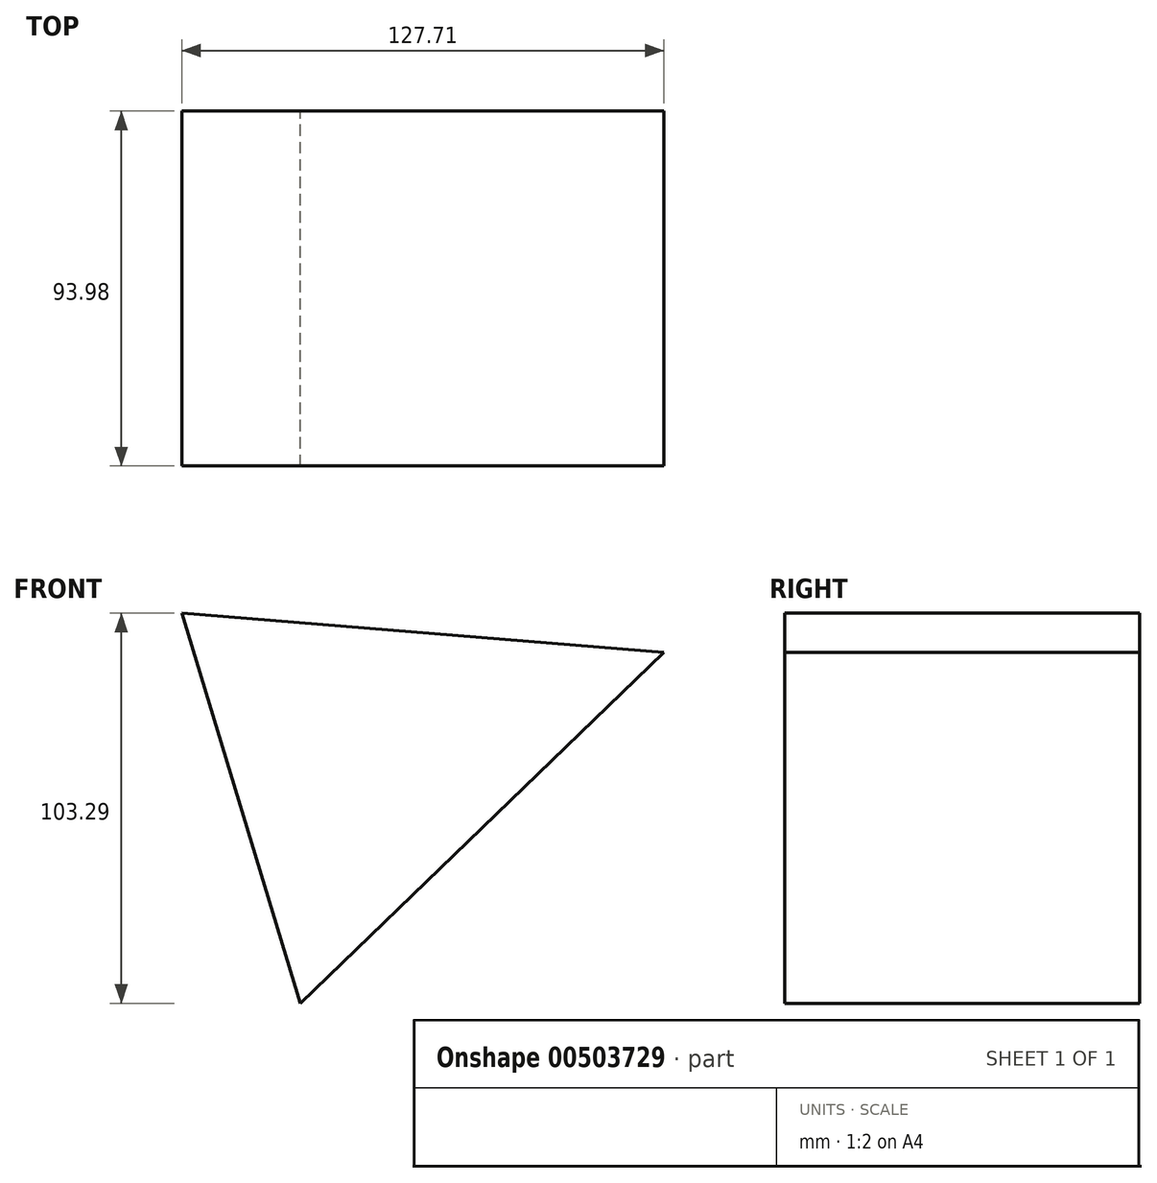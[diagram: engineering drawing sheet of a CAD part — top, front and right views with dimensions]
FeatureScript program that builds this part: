
annotation { "Feature Type Name" : "Feature", "Feature Type Description" : "" }
export const myFeature = defineFeature(function(context is Context, id is Id, definition is map)
    precondition{}
    {
        {
            var Q0;
            Q0=qCreatedBy(makeId("Front.planeOp"),FACE);
            var sketch = newSketch(context, id + "F0", { "sketchPlane" : qUnion([Q0])});
            skLineSegment(sketch, "E0", {"start": v(66.48, 16.82) * mm, "end": v(-29.87, -76.14) * mm});
            skLineSegment(sketch, "E1", {"start": v(-29.87, -76.14) * mm, "end": v(-61.23, 27.15) * mm});
            skLineSegment(sketch, "E2", {"start": v(-61.23, 27.15) * mm, "end": v(66.48, 16.82) * mm});
            skSolve(sketch);
        }
        {
            var Q0;
            Q0=makeQuery(id+"F0.imprint","IMPRINT",FACE,{"disambiguationData":[TD([[makeQuery(id+"F0.imprint","IMPRINT",EDGE,{"derivedFrom":sQuery(id+"F0.wireOp",EDGE,"E0")}),-1.0]])]});
            extrude(context, id + "F1", {"entities" : qUnion([Q0]), "depth" : 93.98 * mm});
        }
    });
